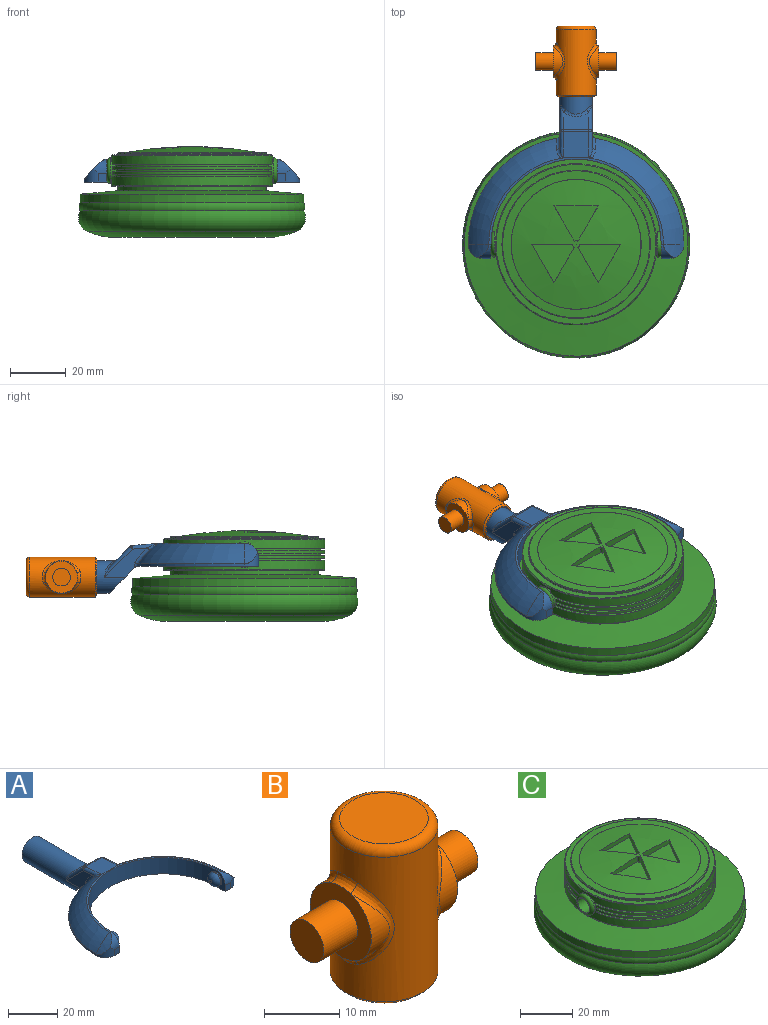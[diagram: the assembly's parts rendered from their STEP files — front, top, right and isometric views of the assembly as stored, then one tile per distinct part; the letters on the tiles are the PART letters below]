
ASSEMBLY  parts=3 mates=2
PART A: 48 faces, bbox 77.3x80.8x18.2 mm
  f0: plane 11.99x9.83mm, normal (0,-0.71,-0.71), area 141.5mm2, adj f1,f2,f9,f30,f43,f46
  f1: plane 15.39x10.49mm, normal (-1,0,0), area 63.5mm2, adj f0,f30,f32,f36,f46,f47
  f2: plane 15.39x10.49mm, normal (1,0,0), area 63.5mm2, adj f0,f30,f34,f39,f43,f44
  f3: plane 9.14x6.37mm, normal (0,0.71,0.71), area 67.6mm2, adj f35,f36,f39,f40
  f4: cylinder r=38.61mm len=37.99mm, axis (0,0,-1), area 42.6mm2, adj f6,f9,f17,f46,f47
  f5: torus R=19.3mm, axis (0,0,-1), area 507.8mm2, adj f10,f11,f12,f29,f42,f44
  f6: torus R=19.3mm, axis (0,0,-1), area 507.8mm2, adj f4,f11,f15,f28,f45,f47
  f7: cylinder r=30.48mm len=60.96mm, axis (0,0,-1), area 746.6mm2, adj f8,f9,f11,f14,f21,f24
  f8: plane 8.13x5.08mm, normal (-1,0,0), area 19.9mm2, adj f7,f9,f13,f19,f24
  f9: plane 77.22x43.73mm, normal (0,0,-1), area 956.2mm2, adj f0,f4,f7,f8,f10,f13,f14,f16
  f10: cylinder r=38.61mm len=37.99mm, axis (0,0,-1), area 42.6mm2, adj f5,f9,f20,f43,f44
  f11: plane 62.55x30.95mm, normal (0,0,1), area 75mm2, adj f5,f6,f7,f18,f19,f27
  f12: cylinder r=22.71mm len=7.33mm, axis (0,1,0), area 24.8mm2, adj f5,f19,f20
  f13: plane 3.05x3.05mm, normal (0,-1,0), area 9.3mm2, adj f8,f9,f19,f20
  f14: plane 8.13x5.08mm, normal (1,0,0), area 19.9mm2, adj f7,f9,f16,f18,f21
  f15: cylinder r=22.71mm len=7.33mm, axis (0,1,0), area 24.8mm2, adj f6,f17,f18
  f16: plane 3.05x3.05mm, normal (0,-1,0), area 9.3mm2, adj f9,f14,f17,f18
  f17: cylinder r=5.08mm len=5.08mm, axis (0,0,-1), area 21.9mm2, adj f4,f9,f15,f16,f18
  f18: cylinder r=5.08mm len=5.08mm, axis (-1,0,0), area 21.9mm2, adj f11,f14,f15,f16,f17
  f19: cylinder r=5.08mm len=5.08mm, axis (-1,0,0), area 21.9mm2, adj f8,f11,f12,f13,f20
  f20: cylinder r=5.08mm len=5.08mm, axis (0,0,-1), area 21.9mm2, adj f9,f10,f12,f13,f19
  f21: cylinder r=3.17mm len=6.35mm, axis (-1,0,0), area 12.7mm2, adj f7,f14,f23
  f22: plane 1.27x1.27mm, normal (1,0,0), area 1.3mm2, adj f23
  f23: torus R=0.64mm, axis (1,0,0), area 56.5mm2, adj f21,f22
  f24: cylinder r=3.17mm len=6.35mm, axis (1,0,0), area 12.7mm2, adj f7,f8,f26
  f25: plane 1.27x1.27mm, normal (-1,0,0), area 1.3mm2, adj f26
  f26: torus R=0.64mm, axis (-1,0,0), area 56.5mm2, adj f24,f25
  f27: plane 9.86x9.36mm, normal (0,0.09,1), area 85.6mm2, adj f11,f28,f29,f32,f34,f35,f42,f45
  f28: plane 1.04x0.17mm, normal (0,-1,0), area 0mm2, adj f6,f27,f45
  f29: plane 1.04x0.17mm, normal (0,-1,0), area 0mm2, adj f5,f27,f42
  f30: cylinder r=5.84mm len=33.01mm, axis (0,-1,0), area 1029.7mm2, adj f0,f1,f2,f31,f38,f40,f41
  f31: plane 11.68x11.68mm, normal (0,1,0), area 107.2mm2, adj f30
  f32: cylinder r=1.27mm len=9.13mm, axis (0,-1,0.09), area 14.4mm2, adj f1,f27,f33,f45
  f33: sphere r=1.27mm, area 1.5mm2, adj f32,f35,f36
  f34: cylinder r=1.27mm len=9.13mm, axis (0,1,-0.09), area 14.4mm2, adj f2,f27,f37,f42
  f35: cylinder r=1.27mm len=9.14mm, axis (-1,0,0), area 8.1mm2, adj f3,f27,f33,f37
  f36: cylinder r=1.27mm len=10.91mm, axis (0,-0.71,0.71), area 23.1mm2, adj f1,f3,f33,f38
  f37: sphere r=1.27mm, area 1.5mm2, adj f34,f35,f39
  f38: bspline ~4.55x2.75mm, area 2.3mm2, adj f30,f36,f40
  f39: cylinder r=1.27mm len=10.91mm, axis (0,0.71,-0.71), area 23.1mm2, adj f2,f3,f37,f41
  f40: bspline ~9.14x2.56mm, area 10.7mm2, adj f3,f30,f38,f41
  f41: bspline ~5.23x3.53mm, area 2.3mm2, adj f30,f39,f40
  f42: bspline ~4.62x3.14mm, area 5.2mm2, adj f5,f27,f29,f34,f44
  f43: cylinder r=1.27mm len=1.74mm, axis (0,0,-1), area 1.9mm2, adj f0,f2,f9,f10,f44
  f44: bspline ~8.6x7.86mm, area 11.9mm2, adj f2,f5,f10,f42,f43
  f45: bspline ~4.62x3.14mm, area 5.2mm2, adj f6,f27,f28,f32,f47
  f46: cylinder r=1.27mm len=1.74mm, axis (0,0,-1), area 1.9mm2, adj f0,f1,f4,f9,f47
  f47: bspline ~8.6x7.86mm, area 11.9mm2, adj f1,f4,f6,f45,f46
PART B: 25 faces, bbox 28.9x15.5x25.4 mm
  f0: cylinder r=5.71mm len=10.81mm, axis (-1,0,0), area 26.2mm2, adj f5,f15
  f1: cylinder r=5.71mm len=10.81mm, axis (-1,0,0), area 26.2mm2, adj f8,f11
  f2: cylinder r=7.14mm len=23.5mm, axis (0,0,-1), area 763.2mm2, adj f9,f10,f11,f12,f13,f14,f15,f16
  f3: plane 11.75x11.75mm, normal (0,0,1), area 108.4mm2, adj f17
  f4: plane 13.02x13.02mm, normal (0,0,-1), area 16.3mm2, adj f22,f24
  f5: plane 11.46x11.46mm, normal (1,0,0), area 70.9mm2, adj f0,f6,f13,f16,f18
  f6: cylinder r=5.71mm len=10.81mm, axis (-1,0,0), area 26.2mm2, adj f5,f14
  f7: cylinder r=5.71mm len=10.81mm, axis (-1,0,0), area 26.2mm2, adj f8,f10
  f8: plane 11.46x11.46mm, normal (-1,0,0), area 70.9mm2, adj f1,f7,f9,f12,f20
  f9: bspline ~4.64x1.73mm, area 6.5mm2, adj f2,f8,f10,f11
  f10: bspline ~13.62x4.91mm, area 20.7mm2, adj f2,f7,f9,f12
  f11: bspline ~13.6x4.87mm, area 20.7mm2, adj f1,f2,f9,f12
  f12: bspline ~4.64x1.73mm, area 6.5mm2, adj f2,f8,f10,f11
  f13: bspline ~4.64x1.73mm, area 6.5mm2, adj f2,f5,f14,f15
  f14: bspline ~13.62x4.91mm, area 20.7mm2, adj f2,f6,f13,f16
  f15: bspline ~13.6x4.87mm, area 20.7mm2, adj f0,f2,f13,f16
  f16: bspline ~4.64x1.73mm, area 6.5mm2, adj f2,f5,f14,f15
  f17: torus R=5.87mm, axis (0,0,1), area 83.8mm2, adj f2,f3
  f18: cylinder r=3.17mm len=6.35mm, axis (-1,0,0), area 126.7mm2, adj f5,f19
  f19: plane 6.35x6.35mm, normal (1,0,0), area 31.7mm2, adj f18
  f20: cylinder r=3.17mm len=6.35mm, axis (1,0,0), area 126.7mm2, adj f8,f21
  f21: plane 6.35x6.35mm, normal (-1,0,0), area 31.7mm2, adj f20
  f22: cylinder r=6.1mm len=22.86mm, axis (0,0,-1), area 875.6mm2, adj f4,f23
  f23: plane 12.19x12.19mm, normal (0,0,-1), area 116.7mm2, adj f22
  f24: cone r=7.14mm half-angle=45deg, axis (0,0,1), area 38.5mm2, adj f2,f4
PART C: 63 faces, bbox 96.3x96.3x32.5 mm
  f0: cylinder r=28.87mm len=57.73mm, axis (0,0,-1), area 595.8mm2, adj f1,f2,f53,f54,f59
  f1: plane 57.14x24.72mm, normal (0,0,1), area 102.1mm2, adj f0,f3,f53,f54
  f2: plane 57.14x24.72mm, normal (0,0,1), area 102mm2, adj f0,f4,f53,f54
  f3: cylinder r=27.6mm len=54.56mm, axis (0,0,-1), area 49.6mm2, adj f1,f6,f53,f54
  f4: cylinder r=27.6mm len=54.56mm, axis (0,0,-1), area 49.6mm2, adj f2,f5,f53,f54
  f5: plane 57.17x24.53mm, normal (0,0,-1), area 101.5mm2, adj f4,f8,f53,f54
  f6: plane 57.17x24.53mm, normal (0,0,-1), area 101.4mm2, adj f3,f7,f53,f54
  f7: cylinder r=28.87mm len=57.06mm, axis (0,0,-1), area 76.6mm2, adj f6,f9,f53,f54
  f8: cylinder r=28.87mm len=57.06mm, axis (0,0,-1), area 76.6mm2, adj f5,f10,f53,f54
  f9: plane 57.01x24.31mm, normal (0,0,1), area 101mm2, adj f7,f11,f53,f54
  f10: plane 57.01x24.31mm, normal (0,0,1), area 101mm2, adj f8,f12,f53,f54
  f11: cylinder r=27.6mm len=54.43mm, axis (0,0,-1), area 49.2mm2, adj f9,f14,f53,f54
  f12: cylinder r=27.6mm len=54.43mm, axis (0,0,-1), area 49.2mm2, adj f10,f13,f53,f54
  f13: plane 57.12x24.36mm, normal (0,0,-1), area 101mm2, adj f12,f16,f53,f54
  f14: plane 57.12x24.36mm, normal (0,0,-1), area 101mm2, adj f11,f15,f53,f54
  f15: cylinder r=28.87mm len=57.09mm, axis (0,0,-1), area 104.9mm2, adj f14,f18,f53,f54
  f16: cylinder r=28.87mm len=57.09mm, axis (0,0,-1), area 104.9mm2, adj f13,f17,f53,f54
  f17: plane 57.1x24.58mm, normal (0,0,1), area 101.7mm2, adj f16,f20,f53,f54
  f18: plane 57.1x24.58mm, normal (0,0,1), area 101.7mm2, adj f15,f19,f53,f54
  f19: cylinder r=27.6mm len=54.61mm, axis (0,0,-1), area 49.8mm2, adj f18,f21,f53,f54
  f20: cylinder r=27.6mm len=54.61mm, axis (0,0,-1), area 49.8mm2, adj f17,f22,f53,f54
  f21: plane 57.29x24.93mm, normal (0,0,-1), area 102.5mm2, adj f19,f23,f53,f54
  f22: plane 57.29x24.93mm, normal (0,0,-1), area 102.4mm2, adj f20,f23,f53,f54
  f23: cylinder r=28.87mm len=57.73mm, axis (0,0,-1), area 543.8mm2, adj f21,f22,f53,f54,f60
  f24: sphere r=135.39mm, area 1385.3mm2, adj f37,f38,f39,f40,f42,f43,f44,f45
  f25: plane 39.33x39.33mm, normal (0,0,-1), area 1214.6mm2, adj f26
  f26: torus R=20.12mm, axis (0,0,-1), area 1429.3mm2, adj f25,f27
  f27: torus R=27.74mm, axis (0,0,-1), area 3542.1mm2, adj f26,f28
  f28: torus R=35.36mm, axis (0,0,-1), area 2180.1mm2, adj f27,f29
  f29: torus R=37.35mm, axis (0,0,-1), area 734.6mm2, adj f28,f30
  f30: cylinder r=40.06mm len=80.11mm, axis (0,0,-1), area 799.1mm2, adj f29,f31
  f31: cone r=26.57mm half-angle=85deg, axis (0,0,-1), area 2833.8mm2, adj f30,f32
  f32: cylinder r=26.57mm len=53.14mm, axis (0,0,-1), area 265mm2, adj f31,f33
  f33: plane 57.23x57.23mm, normal (0,0,-1), area 354.5mm2, adj f32,f59
  f34: cone r=26.57mm half-angle=87deg, axis (0,0,-1), area 475.4mm2, adj f61,f62
  f35: cylinder r=26.57mm len=53.14mm, axis (0,0,-1), area 92.3mm2, adj f36,f61
  f36: plane 57.23x57.23mm, normal (0,0,1), area 354.5mm2, adj f35,f60
  f37: plane 12.65x7.3mm, normal (-0.87,0.5,0), area 32.2mm2, adj f24,f38,f40,f41
  f38: cylinder r=1.27mm len=2.53mm, axis (0,0,1), area 3.4mm2, adj f24,f37,f39,f41
  f39: plane 14.61x2.53mm, normal (0,-1,0), area 32.2mm2, adj f24,f38,f40,f41
  f40: plane 13.75x7.94mm, normal (0.87,0.5,0), area 28mm2, adj f24,f37,f39,f41
  f41: plane 15.24x13.75mm, normal (0,0,1), area 108.3mm2, adj f37,f38,f39,f40
  f42: cylinder r=1.27mm len=2.53mm, axis (0,0,1), area 3.4mm2, adj f24,f43,f45,f46
  f43: plane 12.65x7.3mm, normal (-0.87,0.5,0), area 32.2mm2, adj f24,f42,f44,f46
  f44: plane 15.88x1.84mm, normal (0,-1,0), area 28mm2, adj f24,f43,f45,f46
  f45: plane 12.65x7.3mm, normal (0.87,0.5,0), area 32.2mm2, adj f24,f42,f44,f46
  f46: plane 15.88x12.65mm, normal (0,0,1), area 108.3mm2, adj f42,f43,f44,f45
  f47: cylinder r=1.27mm len=2.53mm, axis (0,0,1), area 3.4mm2, adj f24,f48,f50,f51
  f48: plane 12.65x7.3mm, normal (0.87,0.5,0), area 32.2mm2, adj f24,f47,f49,f51
  f49: plane 13.75x7.94mm, normal (-0.87,0.5,0), area 28mm2, adj f24,f48,f50,f51
  f50: plane 14.61x2.53mm, normal (0,-1,0), area 32.2mm2, adj f24,f47,f49,f51
  f51: plane 15.24x13.75mm, normal (0,0,1), area 108.3mm2, adj f47,f48,f49,f50
  f52: plane 6.6x6.6mm, normal (1,0,0), area 2.6mm2, adj f57,f58
  f53: cylinder r=4.57mm len=9.14mm, axis (-1,0,0), area 23.7mm2, adj f0,f1,f2,f3,f4,f5,f6,f7
  f54: cylinder r=4.57mm len=9.14mm, axis (-1,0,0), area 20.5mm2, adj f0,f1,f2,f3,f4,f5,f6,f7
  f55: plane 6.6x6.6mm, normal (-1,0,0), area 2.6mm2, adj f56,f58
  f56: torus R=3.3mm, axis (1,0,0), area 51.5mm2, adj f54,f55
  f57: torus R=3.3mm, axis (1,0,0), area 51.5mm2, adj f52,f53
  f58: cylinder r=3.17mm len=60.96mm, axis (1,0,0), area 1216.1mm2, adj f52,f55
  f59: torus R=28.61mm, axis (0,0,1), area 72.1mm2, adj f0,f33
  f60: torus R=28.61mm, axis (0,0,-1), area 72.1mm2, adj f23,f36
  f61: torus R=26.31mm, axis (0,0,1), area 64.2mm2, adj f34,f35
  f62: torus R=23.29mm, axis (0,0,1), area 4.5mm2, adj f24,f34
PLACE A t=(32.34,27.52,20.85)mm
PLACE B rot(axis=(-1,0,0),90deg) t=(32.34,80.3,16.88)mm
PLACE C t=(32.34,27.52,33.52)mm
MATE revolute A.f24 <-> C.f53  axis (-1,0,0) through (62.82,27.52,24.92)mm
MATE revolute B.f2 <-> A.f30  axis (0,-1,0) through (32.34,103.16,16.88)mm
